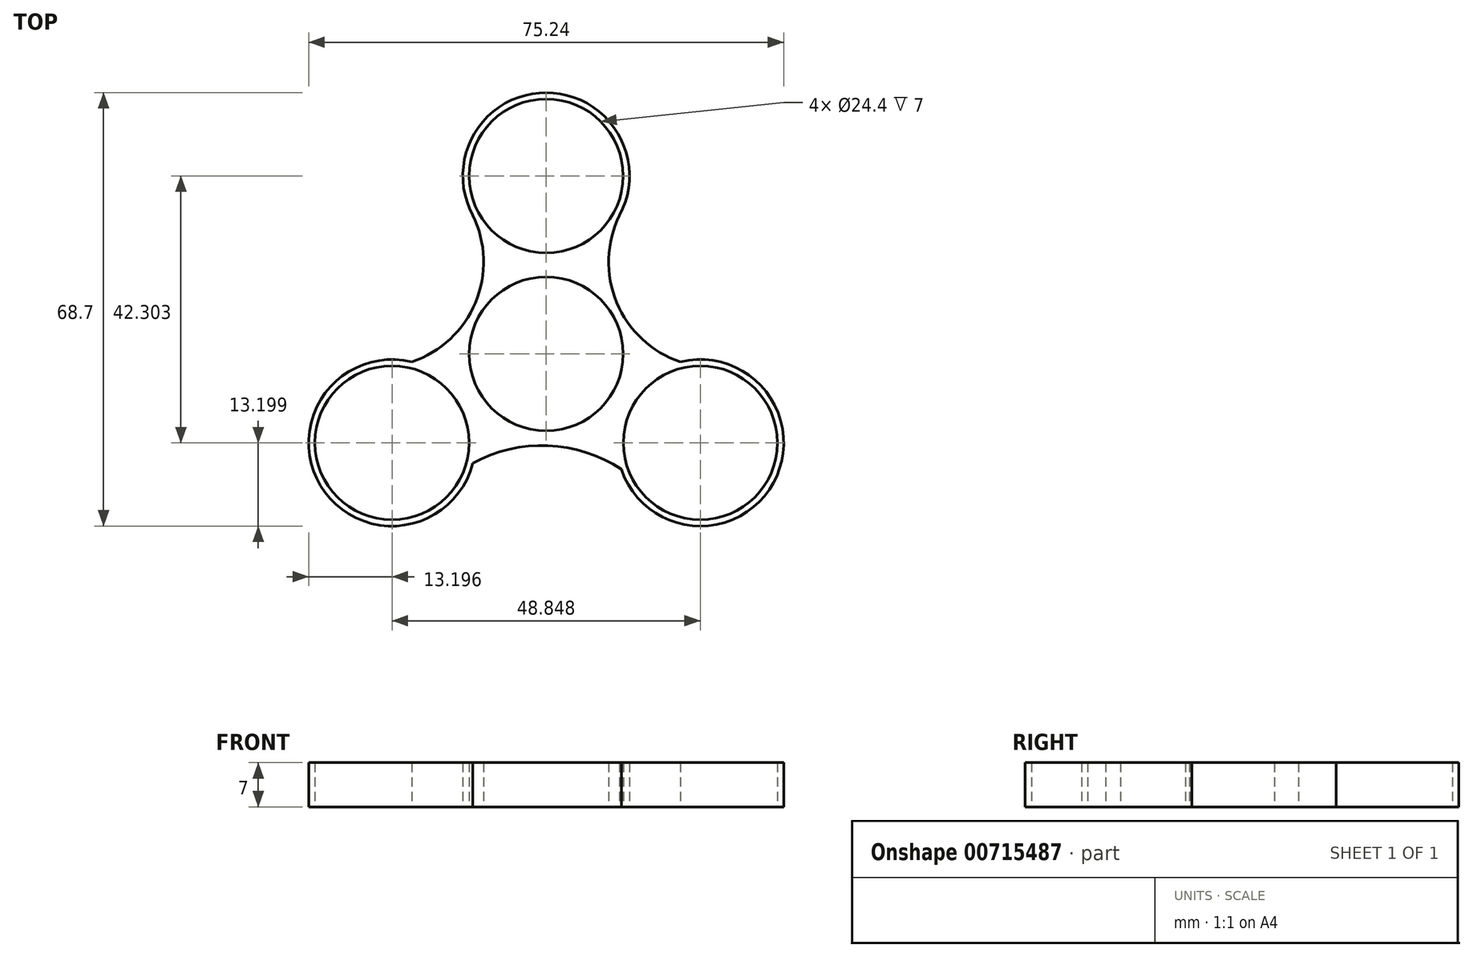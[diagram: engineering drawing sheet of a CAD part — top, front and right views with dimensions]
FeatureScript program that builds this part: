
annotation { "Feature Type Name" : "Feature", "Feature Type Description" : "" }
export const myFeature = defineFeature(function(context is Context, id is Id, definition is map)
    precondition{}
    {
        {
            var Q0;
            Q0=qCreatedBy(makeId("Top.planeOp"),FACE);
            var sketch = newSketch(context, id + "F0", { "sketchPlane" : qUnion([Q0])});
            skCircle(sketch, "E0", {"center": v(0, 0) * mm, "radius": 12.2 * mm});
            skCircle(sketch, "E1", {"center": v(0, 28.2) * mm, "radius": 12.2 * mm});
            skCircle(sketch, "E2.1.0", {"center": v(-24.42, -14.1) * mm, "radius": 12.2 * mm});
            skCircle(sketch, "E2.2.0", {"center": v(24.42, -14.1) * mm, "radius": 12.2 * mm});
            skArc(sketch, "E3", {"start": v(11.63, 21.96) * mm, "mid": v(0, 41.4) * mm, "end": v(-11.63, 21.96) * mm});
            skArc(sketch, "E4.1.0", {"start": v(-21.28, -1.28) * mm, "mid": v(-35.74, -20.9) * mm, "end": v(-11.63, -17.35) * mm});
            skArc(sketch, "E4.2.0", {"start": v(11.91, -18.3) * mm, "mid": v(35.99, -20.47) * mm, "end": v(21.28, -1.28) * mm});
            skArc(sketch, "E5", {"start": v(-21.28, -1.28) * mm, "mid": v(-11.19, 8.15) * mm, "end": v(-11.63, 21.96) * mm});
            skArc(sketch, "E6", {"start": v(11.63, 21.96) * mm, "mid": v(11.17, 8.15) * mm, "end": v(21.28, -1.28) * mm});
            skArc(sketch, "E7", {"start": v(11.91, -18.3) * mm, "mid": v(0.27, -14.54) * mm, "end": v(-11.63, -17.35) * mm});
            skSolve(sketch);
        }
        {
            var Q0;
            Q0 = qSketchRegion(id + "F0", true);
            extrude(context, id + "F1", {"entities" : qUnion([Q0]), "depth" : 7 * mm, "offsetDistance" : 25 * mm});
        }
    });
